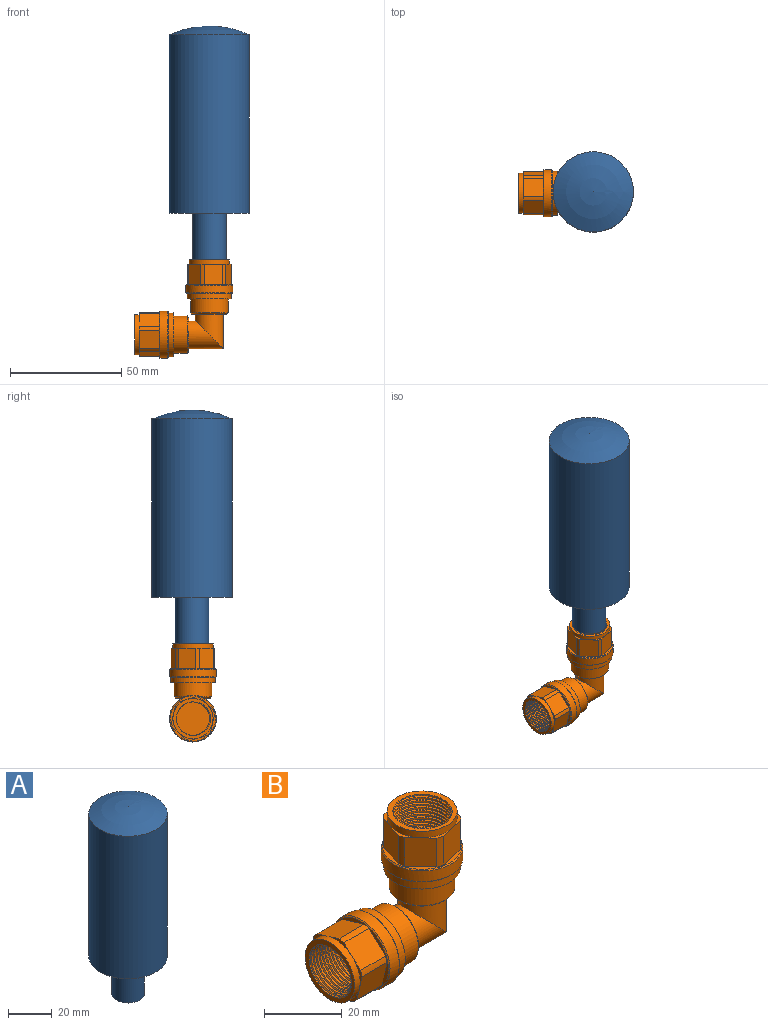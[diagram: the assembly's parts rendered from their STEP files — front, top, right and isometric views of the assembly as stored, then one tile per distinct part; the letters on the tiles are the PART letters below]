
ASSEMBLY  parts=2 mates=1
PART A: 5 faces, bbox 36x36x105 mm
  f0: plane 15x15mm, normal (0,0,-1), area 176.7mm2, adj f1
  f1: cylinder r=7.5mm len=21mm, axis (0,0,1), area 989.6mm2, adj f0,f2
  f2: plane 36x36mm, normal (0,0,-1), area 841.2mm2, adj f1,f3
  f3: cylinder r=18mm len=80mm, axis (0,0,1), area 9047.8mm2, adj f2,f4
  f4: sphere r=42.5mm, area 1068.1mm2, adj f3
PART B: 84 faces, bbox 44.6x21.2x44.6 mm
  f0: cylinder r=6.25mm len=15.5mm, axis (0,0,1), area 363.2mm2, adj f13,f36
  f1: cylinder r=7.5mm len=15.26mm, axis (0,0,1), area 296.8mm2, adj f12,f24,f34,f35
  f2: cylinder r=9.91mm len=9.06mm, axis (0,0,1), area 16.4mm2, adj f8,f20,f29,f30
  f3: cylinder r=9.91mm len=9.06mm, axis (0,0,1), area 16.4mm2, adj f9,f20,f28,f29
  f4: cylinder r=9.91mm len=9.06mm, axis (0,0,1), area 16.4mm2, adj f10,f20,f27,f28
  f5: cylinder r=9.91mm len=9.06mm, axis (0,0,1), area 16.4mm2, adj f11,f20,f26,f27
  f6: cylinder r=9.91mm len=9.06mm, axis (0,0,1), area 16.4mm2, adj f20,f22,f25,f26
  f7: plane 8.78x3.22mm, normal (0,0,1), area 3.9mm2, adj f21,f23,f25,f30
  f8: plane 6.6x6.12mm, normal (0,0,1), area 3.9mm2, adj f2,f23,f29,f30
  f9: plane 8.6x3.58mm, normal (0,0,1), area 3.9mm2, adj f3,f23,f28,f29
  f10: plane 8.78x3.22mm, normal (0,0,1), area 3.9mm2, adj f4,f23,f27,f28
  f11: plane 6.6x6.12mm, normal (0,0,1), area 3.9mm2, adj f5,f23,f26,f27
  f12: plane 15x15mm, normal (0,0,1), area 176.7mm2, adj f1,f33
  f13: plane 15.99x15.99mm, normal (0,0,-1), area 67.4mm2, adj f0,f14,f33,f34,f35
  f14: cone r=8.43mm half-angle=45deg, axis (0,0,1), area 39.5mm2, adj f13,f15,f34,f35
  f15: cylinder r=8.43mm len=16.85mm, axis (0,0,1), area 331.1mm2, adj f14,f16
  f16: plane 19.82x19.82mm, normal (0,0,-1), area 85.5mm2, adj f15,f17
  f17: cylinder r=9.91mm len=19.82mm, axis (0,0,1), area 151mm2, adj f16,f18
  f18: plane 20.4x20.4mm, normal (0,0,-1), area 18.2mm2, adj f17,f31
  f19: cylinder r=10.5mm len=21mm, axis (0,0,1), area 223.9mm2, adj f31,f32
  f20: plane 20.4x20.4mm, normal (0,0,1), area 48.8mm2, adj f2,f3,f4,f5,f6,f21,f25,f26
  f21: cylinder r=9.91mm len=9.06mm, axis (0,0,1), area 16.4mm2, adj f7,f20,f25,f30
  f22: plane 8.6x3.58mm, normal (0,0,1), area 3.9mm2, adj f6,f23,f25,f26
  f23: cylinder r=9mm len=18mm, axis (0,0,1), area 114.3mm2, adj f7,f8,f9,f10,f11,f22,f24
  f24: plane 18.19x18.19mm, normal (0,0,1), area 72.7mm2, adj f1,f23,f34,f35
  f25: plane 9.06x6.09mm, normal (0.73,0.68,0), area 75.2mm2, adj f6,f7,f20,f21,f22
  f26: plane 9.06x8.09mm, normal (-0.22,0.98,0), area 75.2mm2, adj f5,f6,f11,f20,f22
  f27: plane 9.06x7.93mm, normal (-0.96,0.3,0), area 75.2mm2, adj f4,f5,f10,f11,f20
  f28: plane 9.06x6.09mm, normal (-0.73,-0.68,0), area 75.2mm2, adj f3,f4,f9,f10,f20
  f29: plane 9.06x8.09mm, normal (0.22,-0.98,0), area 75.2mm2, adj f2,f3,f8,f9,f20
  f30: plane 9.06x7.93mm, normal (0.96,-0.3,0), area 75.2mm2, adj f2,f7,f8,f20,f21
  f31: cone r=10.5mm half-angle=45deg, axis (0,0,1), area 27.6mm2, adj f18,f19
  f32: cone r=10.2mm half-angle=45deg, axis (0,0,-1), area 27.6mm2, adj f19,f20
  f33: cylinder r=7.5mm len=15mm, axis (0,0,-1), area 219.5mm2, adj f12,f13,f34,f35
  f34: bspline ~24.96x18.33mm, area 572.6mm2, adj f1,f13,f14,f24,f33,f35
  f35: bspline ~24.93x18.33mm, area 553.9mm2, adj f1,f13,f14,f24,f33,f34
  f36: cylinder r=6.25mm len=15.5mm, axis (-1,0,0), area 363.2mm2, adj f0,f49
  f37: cylinder r=7.5mm len=15.26mm, axis (-1,0,0), area 444.8mm2, adj f48,f60,f70,f71
  f38: cylinder r=9.91mm len=9.06mm, axis (-1,0,0), area 16.4mm2, adj f44,f56,f65,f66
  f39: cylinder r=9.91mm len=9.06mm, axis (-1,0,0), area 16.4mm2, adj f45,f56,f64,f65
  f40: cylinder r=9.91mm len=9.06mm, axis (-1,0,0), area 16.4mm2, adj f46,f56,f63,f64
  f41: cylinder r=9.91mm len=9.06mm, axis (-1,0,0), area 16.4mm2, adj f47,f56,f62,f63
  f42: cylinder r=9.91mm len=9.06mm, axis (-1,0,0), area 16.4mm2, adj f56,f58,f61,f62
  f43: plane 8.78x3.22mm, normal (-1,0,0), area 3.9mm2, adj f57,f59,f61,f66
  f44: plane 6.6x6.12mm, normal (-1,0,0), area 3.9mm2, adj f38,f59,f65,f66
  f45: plane 8.6x3.58mm, normal (-1,0,0), area 3.9mm2, adj f39,f59,f64,f65
  f46: plane 8.78x3.22mm, normal (-1,0,0), area 3.9mm2, adj f40,f59,f63,f64
  f47: plane 6.6x6.12mm, normal (-1,0,0), area 3.9mm2, adj f41,f59,f62,f63
  f48: plane 15x15mm, normal (-1,0,0), area 176.7mm2, adj f37,f69
  f49: plane 15.99x15.99mm, normal (1,0,0), area 67.4mm2, adj f36,f50,f69,f70,f71
  f50: cone r=8.43mm half-angle=45deg, axis (-1,0,0), area 39.5mm2, adj f49,f51,f70,f71
  f51: cylinder r=8.43mm len=16.85mm, axis (-1,0,0), area 331.1mm2, adj f50,f52
  f52: plane 19.82x19.82mm, normal (1,0,0), area 85.5mm2, adj f51,f53
  f53: cylinder r=9.91mm len=19.82mm, axis (-1,0,0), area 151mm2, adj f52,f54
  f54: plane 20.4x20.4mm, normal (1,0,0), area 18.2mm2, adj f53,f67
  f55: cylinder r=10.5mm len=21mm, axis (-1,0,0), area 223.9mm2, adj f67,f68
  f56: plane 20.4x20.4mm, normal (-1,0,0), area 48.8mm2, adj f38,f39,f40,f41,f42,f57,f61,f62
  f57: cylinder r=9.91mm len=9.06mm, axis (-1,0,0), area 16.4mm2, adj f43,f56,f61,f66
  f58: plane 8.6x3.58mm, normal (-1,0,0), area 3.9mm2, adj f42,f59,f61,f62
  f59: cylinder r=9mm len=18mm, axis (-1,0,0), area 114.3mm2, adj f43,f44,f45,f46,f47,f58,f60
  f60: plane 18.19x18.19mm, normal (-1,0,0), area 72.7mm2, adj f37,f59,f70,f71
  f61: plane 9.06x6.09mm, normal (0,0.68,-0.73), area 75.2mm2, adj f42,f43,f56,f57,f58
  f62: plane 9.06x8.09mm, normal (0,0.98,0.22), area 75.2mm2, adj f41,f42,f47,f56,f58
  f63: plane 9.06x7.93mm, normal (0,0.3,0.96), area 75.2mm2, adj f40,f41,f46,f47,f56
  f64: plane 9.06x6.09mm, normal (0,-0.68,0.73), area 75.2mm2, adj f39,f40,f45,f46,f56
  f65: plane 9.06x8.09mm, normal (0,-0.98,-0.22), area 75.2mm2, adj f38,f39,f44,f45,f56
  f66: plane 9.06x7.93mm, normal (0,-0.3,-0.96), area 75.2mm2, adj f38,f43,f44,f56,f57
  f67: cone r=10.5mm half-angle=45deg, axis (-1,0,0), area 27.6mm2, adj f54,f55
  f68: cone r=10.2mm half-angle=45deg, axis (1,0,0), area 27.6mm2, adj f55,f56
  f69: cylinder r=7.5mm len=15mm, axis (1,0,0), area 210.7mm2, adj f48,f49,f70,f71
  f70: bspline ~24.96x18.33mm, area 572.6mm2, adj f37,f49,f50,f60,f69,f71
  f71: bspline ~24.93x18.33mm, area 553.9mm2, adj f37,f49,f50,f60,f69,f70
  f72: cylinder r=5.35mm len=12.37mm, axis (0,0,1), area 236mm2, adj f73,f78
  f73: plane 10.7x10.7mm, normal (0,0,-1), area 26.3mm2, adj f72,f77
  f74: plane 7.6x7.6mm, normal (0,0,-1), area 45.4mm2, adj f75
  f75: cylinder r=3.8mm len=9.27mm, axis (0,0,1), area 160.4mm2, adj f74,f76,f81
  f76: cone r=4.5mm half-angle=35deg, axis (0,0,1), area 11.3mm2, adj f75,f77,f82
  f77: cylinder r=4.5mm len=9mm, axis (0,0,1), area 174.1mm2, adj f73,f76,f83
  f78: cylinder r=5.35mm len=12.37mm, axis (-1,0,0), area 236mm2, adj f72,f79
  f79: plane 10.7x10.7mm, normal (1,0,0), area 26.3mm2, adj f78,f83
  f80: plane 7.6x7.6mm, normal (1,0,0), area 45.4mm2, adj f81
  f81: cylinder r=3.8mm len=9.27mm, axis (-1,0,0), area 160.4mm2, adj f75,f80,f82
  f82: cone r=4.5mm half-angle=35deg, axis (-1,0,0), area 11.3mm2, adj f76,f81,f83
  f83: cylinder r=4.5mm len=9mm, axis (-1,0,0), area 174.1mm2, adj f77,f79,f82
PLACE A at identity fixed
PLACE B t=(0.02,-0.44,-21)mm
MATE slider A.f1 <-> B.f24  axis (0,0,-1) through (0,0,-21)mm
